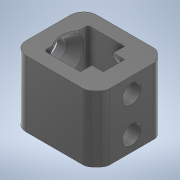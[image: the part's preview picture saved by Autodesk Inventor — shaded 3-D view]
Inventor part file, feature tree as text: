
AUTODESK INVENTOR PART (.ipt)
format: ipt  version: 2020 (Build 240168000, 168)  size: 626,688 bytes
history: native  units: mm
features: extrude x3, chamfer x3, sketch x3
ambient origin geometry x8: Origin, YZ Plane, XZ Plane, XY Plane, X Axis, Y Axis, Z Axis, Center Point
bodies: Volumenkörper1 (feature_tree)
feature tree (9):
  extrude  "Extrusion1"  Depth=3.0mm
  extrude  "Extrusion2"  Depth=2.0mm
  extrude  "Extrusion6"  Depth=4.0mm
  chamfer  "Fase2"  Distance=15.0mm
  chamfer  "Fase3"  Distance=4.2mm
  chamfer  "Fase4"  Distance=8.0mm
  sketch  "Skizze1"  dims[d1=18.9mm d2=3.0mm]
  sketch  "Skizze2"  dims[d3=10.0mm d6=2.0mm]
  sketch  "Skizze7"  dims[d10=3.0mm d11=4.0mm d14=15.0mm d15=0.0mm d16=4.2mm d17=8.0mm d18=0.0mm d19=0.0mm d36=3.0mm d37=4.0mm d41=7.0mm d42=7.0mm d43=3.0mm d44=0.0mm d45=0.4mm d46=2.0mm d47=45.0deg d48=2.0mm d49=2.0mm d50=45.0deg d51=0.5mm d52=2.0mm d53=45.0deg]
